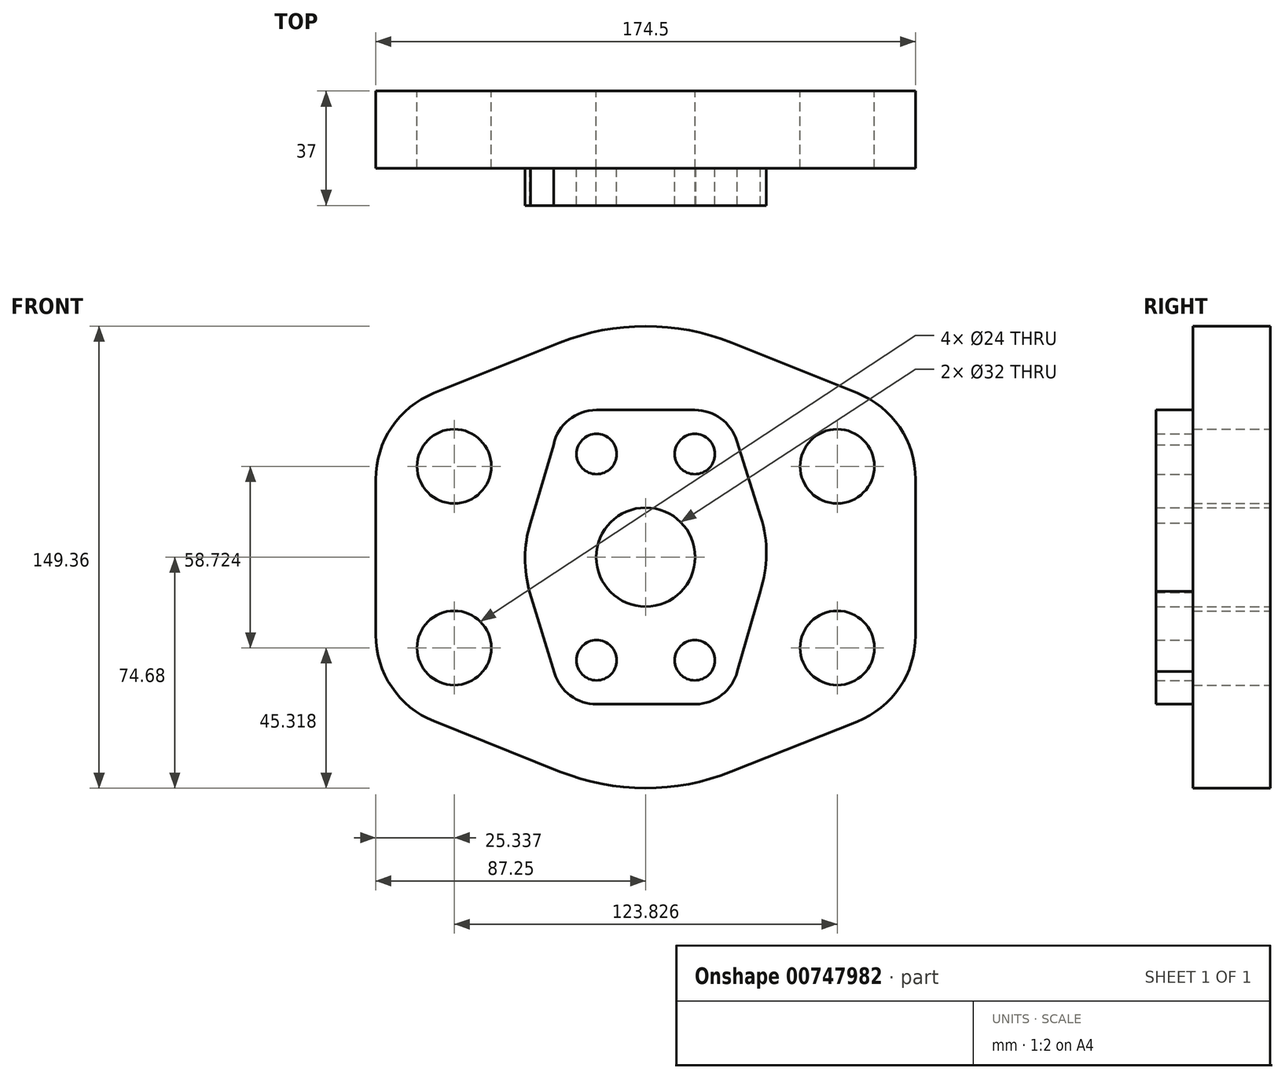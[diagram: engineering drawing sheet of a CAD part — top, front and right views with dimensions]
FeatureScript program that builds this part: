
annotation { "Feature Type Name" : "Feature", "Feature Type Description" : "" }
export const myFeature = defineFeature(function(context is Context, id is Id, definition is map)
    precondition{}
    {
        {
            var Q0;
            Q0=qCreatedBy(makeId("Front.planeOp"),FACE);
            var sketch = newSketch(context, id + "F0", { "sketchPlane" : qUnion([Q0])});
            skCircle(sketch, "E0", {"center": v(-61.91, 29.36) * mm, "radius": 12 * mm});
            skCircle(sketch, "E1.0.1.0", {"center": v(-61.91, -29.36) * mm, "radius": 12 * mm});
            skCircle(sketch, "E1.1.0.0", {"center": v(61.91, 29.36) * mm, "radius": 12 * mm});
            skCircle(sketch, "E1.1.1.0", {"center": v(61.91, -29.36) * mm, "radius": 12 * mm});
            skLineSegment(sketch, "E1.direction1", {"start": v(-61.91, 29.36) * mm, "end": v(61.91, 29.36) * mm, "construction": true});
            skLineSegment(sketch, "E1.direction2", {"start": v(-61.91, 29.36) * mm, "end": v(-61.91, -29.36) * mm, "construction": true});
            skCircle(sketch, "E2", {"center": v(0, 0) * mm, "radius": 16 * mm});
            skLineSegment(sketch, "E3.left", {"start": v(-87.25, -25.18) * mm, "end": v(-87.25, 25.18) * mm});
            skLineSegment(sketch, "E3.right", {"start": v(87.25, -25.31) * mm, "end": v(87.25, 25.18) * mm});
            skPoint(sketch, "E4.visualSharp", {"position": v(-87.25, 57.5) * mm});
            skArc(sketch, "E4.filletArc", {"start": v(-68.41, 53.02) * mm, "mid": v(-82.1, 41.99) * mm, "end": v(-87.25, 25.18) * mm});
            skPoint(sketch, "E5.visualSharp", {"position": v(-87.25, -57.5) * mm});
            skArc(sketch, "E5.filletArc", {"start": v(-87.25, -25.18) * mm, "mid": v(-82.1, -41.99) * mm, "end": v(-68.41, -53.02) * mm});
            skPoint(sketch, "E6.visualSharp", {"position": v(87.25, -57.5) * mm});
            skArc(sketch, "E6.filletArc", {"start": v(68.34, -53.19) * mm, "mid": v(82.07, -42.15) * mm, "end": v(87.25, -25.31) * mm});
            skPoint(sketch, "E7.visualSharp", {"position": v(87.25, 57.5) * mm});
            skArc(sketch, "E7.filletArc", {"start": v(87.25, 25.18) * mm, "mid": v(82.1, 41.99) * mm, "end": v(68.41, 53.02) * mm});
            skLineSegment(sketch, "E8", {"start": v(-68.41, 53.02) * mm, "end": v(-27.8, 69.31) * mm});
            skLineSegment(sketch, "E9", {"start": v(68.41, 53.02) * mm, "end": v(27.8, 69.31) * mm});
            skLineSegment(sketch, "E10", {"start": v(68.34, -53.19) * mm, "end": v(27.6, -69.39) * mm});
            skLineSegment(sketch, "E11", {"start": v(-68.41, -53.02) * mm, "end": v(-27.8, -69.31) * mm});
            skArc(sketch, "E12.trimOffspring", {"start": v(27.8, 69.31) * mm, "mid": v(0, 74.68) * mm, "end": v(-27.8, 69.31) * mm});
            skArc(sketch, "E13.trimOffspring", {"start": v(-27.8, -69.31) * mm, "mid": v(-0.1, -74.68) * mm, "end": v(27.6, -69.39) * mm});
            skSolve(sketch);
        }
        {
            var Q0;
            Q0=makeQuery(id+"F0.imprint","IMPRINT",FACE,{"disambiguationData":[TD([[makeQuery(id+"F0.imprint","IMPRINT",EDGE,{"derivedFrom":sQuery(id+"F0.wireOp",EDGE,"E0")}),-1.0]])]});
            extrude(context, id + "F1", {"entities" : qUnion([Q0]), "depth" : 25 * mm, "offsetDistance" : 25 * mm});
        }
        {
            var Q0;
            Q0=makeQuery(id+"F1.opExtrude","CAP_FACE",FACE,{"disambiguationData":[OSD([sQuery(id+"F0.wireOp",EDGE,"E0"),sQuery(id+"F0.wireOp",EDGE,"E1.0.1.0"),sQuery(id+"F0.wireOp",EDGE,"E1.1.0.0"),sQuery(id+"F0.wireOp",EDGE,"E1.1.1.0"),sQuery(id+"F0.wireOp",EDGE,"E2"),sQuery(id+"F0.wireOp",EDGE,"E3.left"),sQuery(id+"F0.wireOp",EDGE,"E3.right"),sQuery(id+"F0.wireOp",EDGE,"E4.filletArc"),sQuery(id+"F0.wireOp",EDGE,"E5.filletArc"),sQuery(id+"F0.wireOp",EDGE,"E6.filletArc"),sQuery(id+"F0.wireOp",EDGE,"E7.filletArc"),sQuery(id+"F0.wireOp",EDGE,"E8"),sQuery(id+"F0.wireOp",EDGE,"E9"),sQuery(id+"F0.wireOp",EDGE,"E10"),sQuery(id+"F0.wireOp",EDGE,"E11"),sQuery(id+"F0.wireOp",EDGE,"E12.trimOffspring"),sQuery(id+"F0.wireOp",EDGE,"E13.trimOffspring")])],"isStart":false});
            var sketch = newSketch(context, id + "F2", { "sketchPlane" : qUnion([Q0])});
            skCircle(sketch, "E14", {"center": v(-15.88, 33.34) * mm, "radius": 6.5 * mm});
            skCircle(sketch, "E15.0.1.0", {"center": v(-15.88, -33.34) * mm, "radius": 6.5 * mm});
            skCircle(sketch, "E15.1.0.0", {"center": v(15.88, 33.34) * mm, "radius": 6.5 * mm});
            skCircle(sketch, "E15.1.1.0", {"center": v(15.88, -33.34) * mm, "radius": 6.5 * mm});
            skLineSegment(sketch, "E15.direction1", {"start": v(-15.88, 33.34) * mm, "end": v(15.88, 33.34) * mm, "construction": true});
            skLineSegment(sketch, "E15.direction2", {"start": v(-15.88, 33.34) * mm, "end": v(-15.88, -33.34) * mm, "construction": true});
            skArc(sketch, "E16.0.1.0", {"start": v(-29.48, -37.48) * mm, "mid": v(-24.34, -44.77) * mm, "end": v(-15.87, -47.56) * mm});
            skArc(sketch, "E16.1.0.0", {"start": v(29.44, 37.61) * mm, "mid": v(24.29, 44.8) * mm, "end": v(15.87, 47.56) * mm});
            skArc(sketch, "E16.1.1.0", {"start": v(15.56, -47.56) * mm, "mid": v(24.44, -44.7) * mm, "end": v(29.63, -36.95) * mm});
            skLineSegment(sketch, "E17", {"start": v(-15.91, 47.56) * mm, "end": v(15.87, 47.56) * mm});
            skLineSegment(sketch, "E18", {"start": v(29.44, 37.61) * mm, "end": v(37.23, 12.9) * mm});
            skLineSegment(sketch, "E19", {"start": v(29.63, -36.95) * mm, "end": v(37.03, -11.05) * mm});
            skLineSegment(sketch, "E20", {"start": v(16.19, -47.56) * mm, "end": v(-15.87, -47.56) * mm});
            skLineSegment(sketch, "E21", {"start": v(-29.48, -37.48) * mm, "end": v(-37.53, -11.05) * mm});
            skLineSegment(sketch, "E22", {"start": v(-29.77, 36.36) * mm, "end": v(-37.27, 11.02) * mm});
            skArc(sketch, "E23.trimOffspring", {"start": v(-37.27, 11.02) * mm, "mid": v(-39, -0.18) * mm, "end": v(-37.43, -11.4) * mm});
            skArc(sketch, "E24.trimOffspring", {"start": v(-15.84, 47.56) * mm, "mid": v(-24.79, 44.42) * mm, "end": v(-29.77, 36.36) * mm});
            skArc(sketch, "E25", {"start": v(37.23, 12.9) * mm, "mid": v(39.02, 0.9) * mm, "end": v(37.03, -11.05) * mm});
            skSolve(sketch);
        }
        {
            var Q0;
            Q0=makeQuery(id+"F2.imprint","IMPRINT",FACE,{"disambiguationData":[TD([[makeQuery(id+"F2.imprint","IMPRINT",EDGE,{"derivedFrom":sQuery(id+"F2.wireOp",EDGE,"E14")}),-1.0]])]});
            extrude(context, id + "F3", {"entities" : qUnion([Q0]), "depth" : 12 * mm, "offsetDistance" : 25 * mm});
        }
    });
